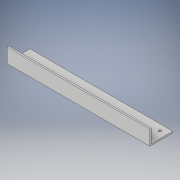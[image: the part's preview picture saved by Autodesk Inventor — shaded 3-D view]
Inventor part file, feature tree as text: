
AUTODESK INVENTOR PART (.ipt)
format: ipt  version: 2018 (Build 220112000, 112)  size: 115,712 bytes
history: native  units: in
note: dims shown in document units (in); Inventor stores cm internally (conversion verified against a paired STEP export)
features: extrude x3, sketch x3
ambient origin geometry x8: Origin, YZ Plane, XZ Plane, XY Plane, X Axis, Y Axis, Z Axis, Center Point
bodies: Solid1 (feature_tree)
feature tree (6):
  extrude  "Extrusion1"  Depth=1.755in
  extrude  "Extrusion2"  Depth=11.0in
  extrude  "Extrusion3"  Depth=1.0in TaperAngle=0.0deg
  sketch  "Sketch1"  dims[d0=11.0in d1=1.755in]
  sketch  "Sketch2"  dims[d2=0.125in d3=0.0in d4=11.0in]
  sketch  "Sketch3"  dims[d5=0.125in d6=1.0in d7=0.0in d10=0.515in d11=0.945in d12=0.2031in d13=0.2031in d14=1.0in d15=0.0in]
